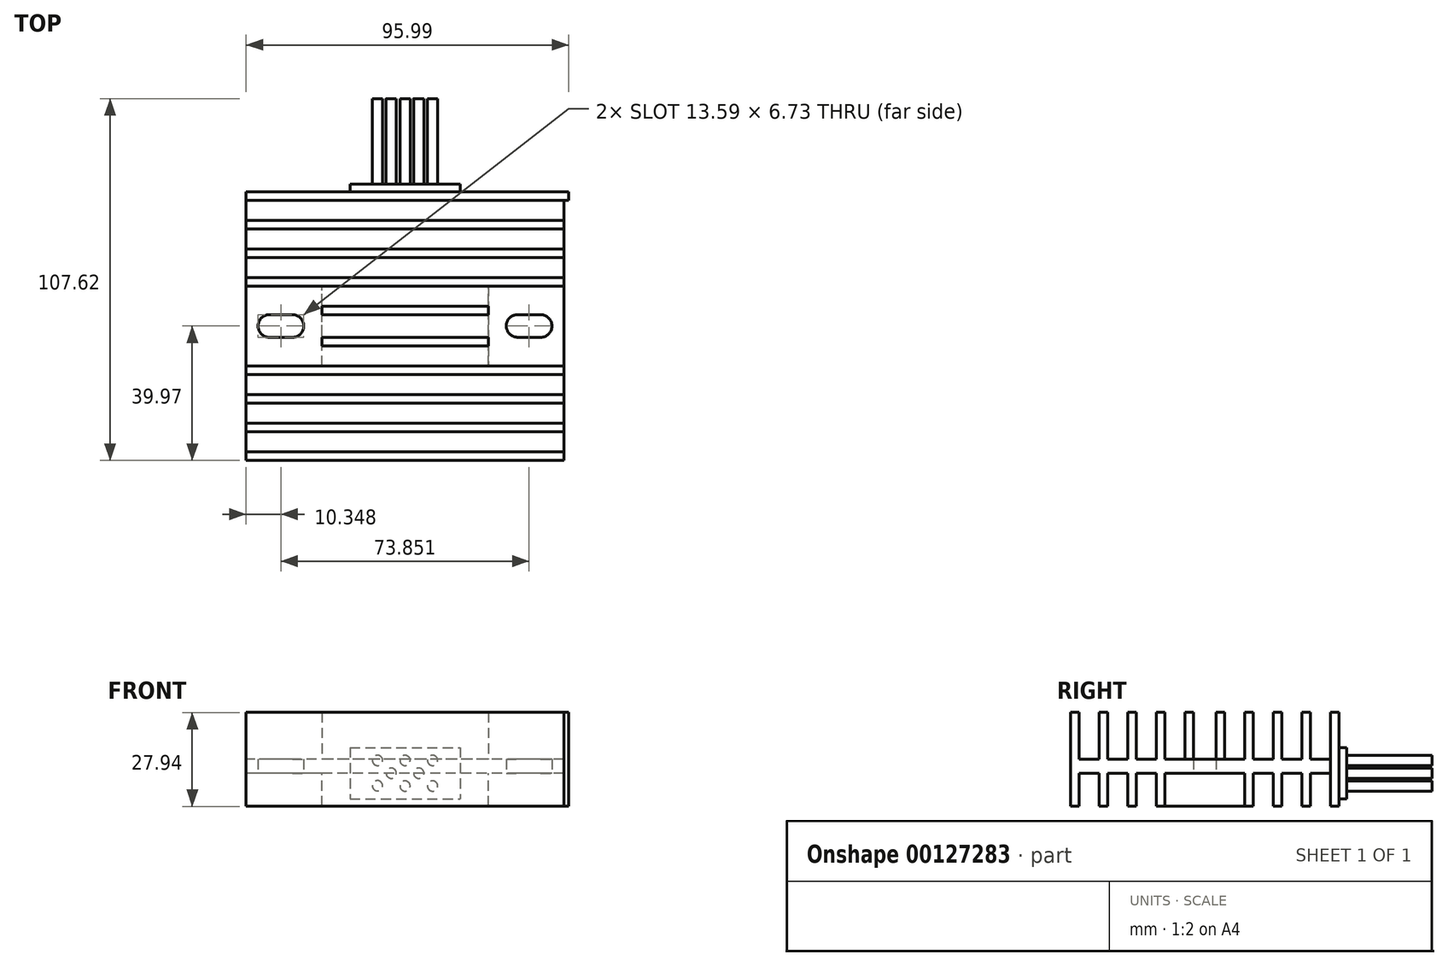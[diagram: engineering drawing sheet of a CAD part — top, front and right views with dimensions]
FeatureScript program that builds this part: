
annotation { "Feature Type Name" : "Feature", "Feature Type Description" : "" }
export const myFeature = defineFeature(function(context is Context, id is Id, definition is map)
    precondition{}
    {
        {
            var Q0;
            Q0=qCreatedBy(makeId("Top.planeOp"),FACE);
            var sketch = newSketch(context, id + "F0", { "sketchPlane" : qUnion([Q0])});
            skLineSegment(sketch, "E0.bottom", {"start": v(47.28, 39.97) * mm, "end": v(-47.28, 39.97) * mm});
            skLineSegment(sketch, "E0.top", {"start": v(47.28, -39.97) * mm, "end": v(-47.28, -39.97) * mm});
            skLineSegment(sketch, "E0.left", {"start": v(47.28, 39.97) * mm, "end": v(47.28, -39.97) * mm});
            skLineSegment(sketch, "E0.right", {"start": v(-47.28, 39.97) * mm, "end": v(-47.28, -39.97) * mm});
            skPoint(sketch, "E0.middle", {"position": v(0, 0) * mm});
            skLineSegment(sketch, "E1.bottom", {"start": v(-33.5, 3.37) * mm, "end": v(-40.36, 3.37) * mm});
            skLineSegment(sketch, "E1.top", {"start": v(-33.5, -3.37) * mm, "end": v(-40.36, -3.37) * mm});
            skPoint(sketch, "E1.middle", {"position": v(-36.93, 0) * mm});
            skArc(sketch, "E2", {"start": v(-40.36, 3.37) * mm, "mid": v(-43.73, 0) * mm, "end": v(-40.36, -3.37) * mm});
            skArc(sketch, "E3", {"start": v(-33.5, -3.37) * mm, "mid": v(-30.14, 0) * mm, "end": v(-33.5, 3.37) * mm});
            skLineSegment(sketch, "E4.bottom", {"start": v(40.36, 3.37) * mm, "end": v(33.5, 3.37) * mm});
            skLineSegment(sketch, "E4.top", {"start": v(40.35, -3.37) * mm, "end": v(33.49, -3.37) * mm});
            skArc(sketch, "E5", {"start": v(40.35, -3.37) * mm, "mid": v(43.71, 0) * mm, "end": v(40.36, 3.37) * mm});
            skArc(sketch, "E6", {"start": v(33.5, 3.37) * mm, "mid": v(30.12, 0) * mm, "end": v(33.49, -3.37) * mm});
            skSolve(sketch);
        }
        {
            var Q0;
            Q0=makeQuery(id+"F0.imprint","IMPRINT",FACE,{"disambiguationData":[TD([[makeQuery(id+"F0.imprint","IMPRINT",EDGE,{"derivedFrom":sQuery(id+"F0.wireOp",EDGE,"E0.bottom")}),1.0]])]});
            extrude(context, id + "F1", {"entities" : qUnion([Q0]), "depth" : 4.11 * mm});
        }
        {
            var Q0;
            Q0=makeQuery(id+"F1.opExtrude","CAP_FACE",FACE,{"disambiguationData":[OSD([sQuery(id+"F0.wireOp",EDGE,"E0.bottom"),sQuery(id+"F0.wireOp",EDGE,"E0.top"),sQuery(id+"F0.wireOp",EDGE,"E0.left"),sQuery(id+"F0.wireOp",EDGE,"E0.right"),sQuery(id+"F0.wireOp",EDGE,"E1.bottom"),sQuery(id+"F0.wireOp",EDGE,"E1.top"),sQuery(id+"F0.wireOp",EDGE,"E2"),sQuery(id+"F0.wireOp",EDGE,"E3"),sQuery(id+"F0.wireOp",EDGE,"E4.bottom"),sQuery(id+"F0.wireOp",EDGE,"E4.top"),sQuery(id+"F0.wireOp",EDGE,"E5"),sQuery(id+"F0.wireOp",EDGE,"E6")])],"isStart":false});
            var sketch = newSketch(context, id + "F2", { "sketchPlane" : qUnion([Q0])});
            skLineSegment(sketch, "E7.bottom", {"start": v(24.77, 39.97) * mm, "end": v(-24.77, 39.97) * mm});
            skLineSegment(sketch, "E7.top", {"start": v(24.77, -39.97) * mm, "end": v(-24.77, -39.97) * mm});
            skLineSegment(sketch, "E7.left", {"start": v(24.77, 39.97) * mm, "end": v(24.77, -39.97) * mm});
            skLineSegment(sketch, "E7.right", {"start": v(-24.77, 39.97) * mm, "end": v(-24.77, -39.97) * mm});
            skPoint(sketch, "E7.middle", {"position": v(0, 0) * mm});
            skLineSegment(sketch, "E8.bottom", {"start": v(-47.28, 39.97) * mm, "end": v(48.7, 39.97) * mm});
            skLineSegment(sketch, "E8.top", {"start": v(-47.28, 37.43) * mm, "end": v(48.7, 37.43) * mm});
            skLineSegment(sketch, "E8.left", {"start": v(-47.28, 39.97) * mm, "end": v(-47.28, 37.43) * mm});
            skLineSegment(sketch, "E8.right", {"start": v(48.7, 39.97) * mm, "end": v(48.7, 37.43) * mm});
            skLineSegment(sketch, "E9.bottom", {"start": v(-47.28, 31.46) * mm, "end": v(47.28, 31.46) * mm});
            skLineSegment(sketch, "E9.top", {"start": v(-47.28, 28.92) * mm, "end": v(47.28, 28.92) * mm});
            skLineSegment(sketch, "E9.left", {"start": v(-47.28, 31.46) * mm, "end": v(-47.28, 28.92) * mm});
            skLineSegment(sketch, "E9.right", {"start": v(47.28, 31.46) * mm, "end": v(47.28, 28.92) * mm});
            skLineSegment(sketch, "E10.bottom", {"start": v(-47.28, 22.95) * mm, "end": v(47.28, 22.95) * mm});
            skLineSegment(sketch, "E10.top", {"start": v(-47.28, 20.4) * mm, "end": v(47.28, 20.4) * mm});
            skLineSegment(sketch, "E10.left", {"start": v(-47.28, 22.95) * mm, "end": v(-47.28, 20.4) * mm});
            skLineSegment(sketch, "E10.right", {"start": v(47.28, 22.95) * mm, "end": v(47.28, 20.4) * mm});
            skLineSegment(sketch, "E11.bottom", {"start": v(-47.28, 14.44) * mm, "end": v(47.28, 14.44) * mm});
            skLineSegment(sketch, "E11.top", {"start": v(-47.28, 11.9) * mm, "end": v(47.28, 11.9) * mm});
            skLineSegment(sketch, "E11.left", {"start": v(-47.28, 14.44) * mm, "end": v(-47.28, 11.9) * mm});
            skLineSegment(sketch, "E11.right", {"start": v(47.28, 14.44) * mm, "end": v(47.28, 11.9) * mm});
            skLineSegment(sketch, "E12.bottom", {"start": v(-24.77, 5.93) * mm, "end": v(24.77, 5.93) * mm});
            skLineSegment(sketch, "E12.top", {"start": v(-24.77, 3.4) * mm, "end": v(24.77, 3.4) * mm});
            skLineSegment(sketch, "E12.left", {"start": v(-24.77, 5.93) * mm, "end": v(-24.77, 3.4) * mm});
            skLineSegment(sketch, "E12.right", {"start": v(24.77, 5.93) * mm, "end": v(24.77, 3.4) * mm});
            skLineSegment(sketch, "E13.bottom", {"start": v(-47.28, -39.97) * mm, "end": v(47.28, -39.97) * mm});
            skLineSegment(sketch, "E13.top", {"start": v(-47.28, -37.43) * mm, "end": v(47.28, -37.43) * mm});
            skLineSegment(sketch, "E13.left", {"start": v(-47.28, -39.97) * mm, "end": v(-47.28, -37.43) * mm});
            skLineSegment(sketch, "E13.right", {"start": v(47.28, -39.97) * mm, "end": v(47.28, -37.43) * mm});
            skLineSegment(sketch, "E14.bottom", {"start": v(-47.28, -31.46) * mm, "end": v(47.28, -31.46) * mm});
            skLineSegment(sketch, "E14.top", {"start": v(-47.28, -28.92) * mm, "end": v(47.28, -28.92) * mm});
            skLineSegment(sketch, "E14.left", {"start": v(-47.28, -31.46) * mm, "end": v(-47.28, -28.92) * mm});
            skLineSegment(sketch, "E14.right", {"start": v(47.28, -31.46) * mm, "end": v(47.28, -28.92) * mm});
            skLineSegment(sketch, "E15.bottom", {"start": v(-47.28, -22.95) * mm, "end": v(47.28, -22.95) * mm});
            skLineSegment(sketch, "E15.top", {"start": v(-47.28, -20.4) * mm, "end": v(47.28, -20.4) * mm});
            skLineSegment(sketch, "E15.left", {"start": v(-47.28, -22.95) * mm, "end": v(-47.28, -20.4) * mm});
            skLineSegment(sketch, "E15.right", {"start": v(47.28, -22.95) * mm, "end": v(47.28, -20.4) * mm});
            skLineSegment(sketch, "E16.bottom", {"start": v(-47.28, -14.44) * mm, "end": v(47.28, -14.44) * mm});
            skLineSegment(sketch, "E16.top", {"start": v(-47.28, -11.9) * mm, "end": v(47.28, -11.9) * mm});
            skLineSegment(sketch, "E16.left", {"start": v(-47.28, -14.44) * mm, "end": v(-47.28, -11.9) * mm});
            skLineSegment(sketch, "E16.right", {"start": v(47.28, -14.44) * mm, "end": v(47.28, -11.9) * mm});
            skLineSegment(sketch, "E17.bottom", {"start": v(-24.77, -5.93) * mm, "end": v(24.77, -5.93) * mm});
            skLineSegment(sketch, "E17.top", {"start": v(-24.77, -3.4) * mm, "end": v(24.77, -3.4) * mm});
            skLineSegment(sketch, "E17.left", {"start": v(-24.77, -5.93) * mm, "end": v(-24.77, -3.4) * mm});
            skLineSegment(sketch, "E17.right", {"start": v(24.77, -5.93) * mm, "end": v(24.77, -3.4) * mm});
            skSolve(sketch);
        }
        {
            var Q0;
            {var subQ5=sQuery(id+"F2.wireOp",EDGE,"E13.right");Q0=makeQuery(id+"F2.imprint","IMPRINT",FACE,{"disambiguationData":[TD([[makeQuery(id+"F2.imprint","IMPRINT",EDGE,{"derivedFrom":subQ5}),-1.0]])]});}
            var Q1;
            {var subQ5=sQuery(id+"F2.wireOp",EDGE,"E8.left");Q1=makeQuery(id+"F2.imprint","IMPRINT",FACE,{"disambiguationData":[TD([[makeQuery(id+"F2.imprint","IMPRINT",EDGE,{"derivedFrom":subQ5}),1.0]])]});}
            var Q2;
            {var subQ5=sQuery(id+"F2.wireOp",EDGE,"E13.left");Q2=makeQuery(id+"F2.imprint","IMPRINT",FACE,{"disambiguationData":[TD([[makeQuery(id+"F2.imprint","IMPRINT",EDGE,{"derivedFrom":subQ5}),1.0]])]});}
            var Q3;
            {var subQ0=sQuery(id+"F2.wireOp",EDGE,"E8.bottom");var subQ1=sQuery(id+"F2.wireOp",EDGE,"E7.left");var subQ2=makeQuery(id+"F2.imprint","INTERSECT",VERTEX,{"derivedFrom":[subQ1,subQ0]});Q3=makeQuery(id+"F2.imprint","IMPRINT",FACE,{"disambiguationData":[TD([[makeQuery(id+"F2.imprint","IMPRINT",EDGE,{"disambiguationData":[TD([[subQ2,-1.0]])],"derivedFrom":subQ1}),-1.0]])]});}
            var Q4;
            {var subQ5=sQuery(id+"F2.wireOp",EDGE,"E9.right");Q4=makeQuery(id+"F2.imprint","IMPRINT",FACE,{"disambiguationData":[TD([[makeQuery(id+"F2.imprint","IMPRINT",EDGE,{"derivedFrom":subQ5}),-1.0]])]});}
            var Q5;
            {var subQ5=sQuery(id+"F2.wireOp",EDGE,"E10.right");Q5=makeQuery(id+"F2.imprint","IMPRINT",FACE,{"disambiguationData":[TD([[makeQuery(id+"F2.imprint","IMPRINT",EDGE,{"derivedFrom":subQ5}),-1.0]])]});}
            var Q6;
            {var subQ5=sQuery(id+"F2.wireOp",EDGE,"E11.right");Q6=makeQuery(id+"F2.imprint","IMPRINT",FACE,{"disambiguationData":[TD([[makeQuery(id+"F2.imprint","IMPRINT",EDGE,{"derivedFrom":subQ5}),-1.0]])]});}
            var Q7;
            {var subQ5=sQuery(id+"F2.wireOp",EDGE,"E16.right");Q7=makeQuery(id+"F2.imprint","IMPRINT",FACE,{"disambiguationData":[TD([[makeQuery(id+"F2.imprint","IMPRINT",EDGE,{"derivedFrom":subQ5}),-1.0]])]});}
            var Q8;
            {var subQ5=sQuery(id+"F2.wireOp",EDGE,"E15.right");Q8=makeQuery(id+"F2.imprint","IMPRINT",FACE,{"disambiguationData":[TD([[makeQuery(id+"F2.imprint","IMPRINT",EDGE,{"derivedFrom":subQ5}),-1.0]])]});}
            var Q9;
            {var subQ5=sQuery(id+"F2.wireOp",EDGE,"E14.right");Q9=makeQuery(id+"F2.imprint","IMPRINT",FACE,{"disambiguationData":[TD([[makeQuery(id+"F2.imprint","IMPRINT",EDGE,{"derivedFrom":subQ5}),-1.0]])]});}
            var Q10;
            {var subQ0=sQuery(id+"F2.wireOp",EDGE,"E13.bottom");var subQ1=sQuery(id+"F2.wireOp",EDGE,"E7.left");var subQ2=makeQuery(id+"F2.imprint","INTERSECT",VERTEX,{"derivedFrom":[subQ1,subQ0]});Q10=makeQuery(id+"F2.imprint","IMPRINT",FACE,{"disambiguationData":[TD([[makeQuery(id+"F2.imprint","IMPRINT",EDGE,{"disambiguationData":[TD([[subQ2,1.0]])],"derivedFrom":subQ1}),-1.0]])]});}
            var Q11;
            {var subQ5=sQuery(id+"F2.wireOp",EDGE,"E9.left");Q11=makeQuery(id+"F2.imprint","IMPRINT",FACE,{"disambiguationData":[TD([[makeQuery(id+"F2.imprint","IMPRINT",EDGE,{"derivedFrom":subQ5}),1.0]])]});}
            var Q12;
            {var subQ5=sQuery(id+"F2.wireOp",EDGE,"E10.left");Q12=makeQuery(id+"F2.imprint","IMPRINT",FACE,{"disambiguationData":[TD([[makeQuery(id+"F2.imprint","IMPRINT",EDGE,{"derivedFrom":subQ5}),1.0]])]});}
            var Q13;
            {var subQ5=sQuery(id+"F2.wireOp",EDGE,"E11.left");Q13=makeQuery(id+"F2.imprint","IMPRINT",FACE,{"disambiguationData":[TD([[makeQuery(id+"F2.imprint","IMPRINT",EDGE,{"derivedFrom":subQ5}),1.0]])]});}
            var Q14;
            {var subQ5=sQuery(id+"F2.wireOp",EDGE,"E16.left");Q14=makeQuery(id+"F2.imprint","IMPRINT",FACE,{"disambiguationData":[TD([[makeQuery(id+"F2.imprint","IMPRINT",EDGE,{"derivedFrom":subQ5}),1.0]])]});}
            var Q15;
            {var subQ5=sQuery(id+"F2.wireOp",EDGE,"E15.left");Q15=makeQuery(id+"F2.imprint","IMPRINT",FACE,{"disambiguationData":[TD([[makeQuery(id+"F2.imprint","IMPRINT",EDGE,{"derivedFrom":subQ5}),1.0]])]});}
            var Q16;
            {var subQ5=sQuery(id+"F2.wireOp",EDGE,"E14.left");Q16=makeQuery(id+"F2.imprint","IMPRINT",FACE,{"disambiguationData":[TD([[makeQuery(id+"F2.imprint","IMPRINT",EDGE,{"derivedFrom":subQ5}),1.0]])]});}
            var Q17;
            {var subQ0=sQuery(id+"F2.wireOp",EDGE,"E9.bottom");var subQ1=sQuery(id+"F2.wireOp",EDGE,"E7.left");var subQ2=makeQuery(id+"F2.imprint","INTERSECT",VERTEX,{"derivedFrom":[subQ1,subQ0]});Q17=makeQuery(id+"F2.imprint","IMPRINT",FACE,{"disambiguationData":[TD([[makeQuery(id+"F2.imprint","IMPRINT",EDGE,{"disambiguationData":[TD([[subQ2,-1.0]])],"derivedFrom":subQ1}),-1.0]])]});}
            var Q18;
            {var subQ0=sQuery(id+"F2.wireOp",EDGE,"E10.bottom");var subQ1=sQuery(id+"F2.wireOp",EDGE,"E7.left");var subQ2=makeQuery(id+"F2.imprint","INTERSECT",VERTEX,{"derivedFrom":[subQ1,subQ0]});Q18=makeQuery(id+"F2.imprint","IMPRINT",FACE,{"disambiguationData":[TD([[makeQuery(id+"F2.imprint","IMPRINT",EDGE,{"disambiguationData":[TD([[subQ2,-1.0]])],"derivedFrom":subQ1}),-1.0]])]});}
            var Q19;
            {var subQ0=sQuery(id+"F2.wireOp",EDGE,"E11.bottom");var subQ1=sQuery(id+"F2.wireOp",EDGE,"E7.left");var subQ2=makeQuery(id+"F2.imprint","INTERSECT",VERTEX,{"derivedFrom":[subQ1,subQ0]});Q19=makeQuery(id+"F2.imprint","IMPRINT",FACE,{"disambiguationData":[TD([[makeQuery(id+"F2.imprint","IMPRINT",EDGE,{"disambiguationData":[TD([[subQ2,-1.0]])],"derivedFrom":subQ1}),-1.0]])]});}
            var Q20;
            {var subQ0=sQuery(id+"F2.wireOp",EDGE,"E16.top");var subQ1=sQuery(id+"F2.wireOp",EDGE,"E7.left");var subQ2=makeQuery(id+"F2.imprint","INTERSECT",VERTEX,{"derivedFrom":[subQ1,subQ0]});Q20=makeQuery(id+"F2.imprint","IMPRINT",FACE,{"disambiguationData":[TD([[makeQuery(id+"F2.imprint","IMPRINT",EDGE,{"disambiguationData":[TD([[subQ2,-1.0]])],"derivedFrom":subQ1}),-1.0]])]});}
            var Q21;
            {var subQ0=sQuery(id+"F2.wireOp",EDGE,"E15.top");var subQ1=sQuery(id+"F2.wireOp",EDGE,"E7.left");var subQ2=makeQuery(id+"F2.imprint","INTERSECT",VERTEX,{"derivedFrom":[subQ1,subQ0]});Q21=makeQuery(id+"F2.imprint","IMPRINT",FACE,{"disambiguationData":[TD([[makeQuery(id+"F2.imprint","IMPRINT",EDGE,{"disambiguationData":[TD([[subQ2,-1.0]])],"derivedFrom":subQ1}),-1.0]])]});}
            var Q22;
            {var subQ0=sQuery(id+"F2.wireOp",EDGE,"E14.top");var subQ1=sQuery(id+"F2.wireOp",EDGE,"E7.left");var subQ2=makeQuery(id+"F2.imprint","INTERSECT",VERTEX,{"derivedFrom":[subQ1,subQ0]});Q22=makeQuery(id+"F2.imprint","IMPRINT",FACE,{"disambiguationData":[TD([[makeQuery(id+"F2.imprint","IMPRINT",EDGE,{"disambiguationData":[TD([[subQ2,-1.0]])],"derivedFrom":subQ1}),-1.0]])]});}
            var Q23;
            Q23=makeQuery(id+"F2.imprint","IMPRINT",FACE,{"disambiguationData":[TD([[makeQuery(id+"F2.imprint","IMPRINT",EDGE,{"derivedFrom":sQuery(id+"F2.wireOp",EDGE,"E12.bottom")}),-1.0]])]});
            var Q24;
            Q24=makeQuery(id+"F2.imprint","IMPRINT",FACE,{"disambiguationData":[TD([[makeQuery(id+"F2.imprint","IMPRINT",EDGE,{"derivedFrom":sQuery(id+"F2.wireOp",EDGE,"E17.bottom")}),1.0]])]});
            var Q25;
            {var subQ3=sQuery(id+"F2.wireOp",EDGE,"E8.right");Q25=makeQuery(id+"F2.imprint","IMPRINT",FACE,{"disambiguationData":[TD([[makeQuery(id+"F2.imprint","IMPRINT",EDGE,{"derivedFrom":subQ3}),-1.0]])]});}
            var Q26;
            {var subQ0=sQuery(id+"F2.wireOp",EDGE,"E8.bottom");var subQ1=sQuery(id+"F2.wireOp",EDGE,"E7.left");var subQ2=makeQuery(id+"F2.imprint","INTERSECT",VERTEX,{"derivedFrom":[subQ1,subQ0]});Q26=makeQuery(id+"F2.imprint","IMPRINT",FACE,{"disambiguationData":[TD([[makeQuery(id+"F2.imprint","IMPRINT",EDGE,{"disambiguationData":[TD([[subQ2,-1.0]])],"derivedFrom":subQ1}),1.0]])]});}
            extrude(context, id + "F3", {"entities" : qUnion([Q0, Q1, Q2, Q3, Q4, Q5, Q6, Q7, Q8, Q9, Q10, Q11, Q12, Q13, Q14, Q15, Q16, Q17, Q18, Q19, Q20, Q21, Q22, Q23, Q24, Q25, Q26]), "operationType" : NewBodyOperationType.ADD, "endBound" : BoundingType.SYMMETRIC, "depth" : 27.94 * mm, "hasSecondDirection" : true, "secondDirectionOppositeDirection" : true, "secondDirectionDepth" : 25.4 * mm});
        }
        {
            var Q0;
            Q0=makeQuery(id+"F3.boolean.opBoolean","MERGE",FACE,{"derivedFrom":[makeQuery(id+"F1.opExtrude","SWEPT_FACE",FACE,{"disambiguationData":[OSD([sQuery(id+"F0.wireOp",EDGE,"E0.bottom")])]}),makeQuery(id+"F3.opExtrude","SWEPT_FACE",FACE,{"disambiguationData":[OSD([sQuery(id+"F2.wireOp",EDGE,"E8.bottom")])]})]});
            var sketch = newSketch(context, id + "F4", { "sketchPlane" : qUnion([Q0])});
            skLineSegment(sketch, "E18.bottom", {"start": v(16.38, 7.62) * mm, "end": v(-16.38, 7.62) * mm});
            skLineSegment(sketch, "E18.top", {"start": v(16.38, -7.62) * mm, "end": v(-16.38, -7.62) * mm});
            skLineSegment(sketch, "E18.left", {"start": v(16.38, 7.62) * mm, "end": v(16.38, -7.62) * mm});
            skLineSegment(sketch, "E18.right", {"start": v(-16.38, 7.62) * mm, "end": v(-16.38, -7.62) * mm});
            skPoint(sketch, "E18.middle", {"position": v(0, 0) * mm});
            skSolve(sketch);
        }
        {
            var Q0;
            Q0=makeQuery(id+"F4.imprint","IMPRINT",FACE,{"disambiguationData":[TD([[makeQuery(id+"F4.imprint","IMPRINT",EDGE,{"derivedFrom":sQuery(id+"F4.wireOp",EDGE,"E18.bottom")}),1.0]])]});
            extrude(context, id + "F5", {"entities" : qUnion([Q0]), "operationType" : NewBodyOperationType.ADD, "depth" : 2.3 * mm});
        }
        {
            var Q0;
            Q0=makeQuery(id+"F5.opExtrude","CAP_FACE",FACE,{"disambiguationData":[OSD([sQuery(id+"F4.wireOp",EDGE,"E18.bottom"),sQuery(id+"F4.wireOp",EDGE,"E18.top"),sQuery(id+"F4.wireOp",EDGE,"E18.left"),sQuery(id+"F4.wireOp",EDGE,"E18.right")])],"isStart":false});
            var sketch = newSketch(context, id + "F6", { "sketchPlane" : qUnion([Q0])});
            skCircle(sketch, "E19", {"center": v(-8.2, 3.8) * mm, "radius": 1.52 * mm});
            skCircle(sketch, "E20", {"center": v(8.2, 3.81) * mm, "radius": 1.52 * mm});
            skCircle(sketch, "E21", {"center": v(4.1, 0) * mm, "radius": 1.52 * mm});
            skCircle(sketch, "E22", {"center": v(-4.1, 0) * mm, "radius": 1.52 * mm});
            skCircle(sketch, "E23", {"center": v(8.2, -3.73) * mm, "radius": 1.52 * mm});
            skCircle(sketch, "E24", {"center": v(-8.2, -3.81) * mm, "radius": 1.52 * mm});
            skCircle(sketch, "E25", {"center": v(0, 3.81) * mm, "radius": 1.52 * mm});
            skCircle(sketch, "E26", {"center": v(0, -3.81) * mm, "radius": 1.52 * mm});
            skSolve(sketch);
        }
        {
            var Q0;
            {var subQ0=sQuery(id+"F0.wireOp",EDGE,"E5");var subQ1=sQuery(id+"F0.wireOp",EDGE,"E1.top");var subQ2=sQuery(id+"F0.wireOp",EDGE,"E1.bottom");var subQ3=sQuery(id+"F0.wireOp",EDGE,"E0.right");var subQ4=sQuery(id+"F0.wireOp",EDGE,"E0.left");var subQ5=sQuery(id+"F0.wireOp",EDGE,"E2");var subQ6=sQuery(id+"F0.wireOp",EDGE,"E3");var subQ7=sQuery(id+"F0.wireOp",EDGE,"E6");var subQ8=sQuery(id+"F0.wireOp",EDGE,"E4.bottom");var subQ9=sQuery(id+"F0.wireOp",EDGE,"E4.top");Q0=makeQuery(id+"F3.boolean.opBoolean","SPLIT",FACE,{"disambiguationData":[TD([makeQuery(id+"F1.opExtrude","SWEPT_FACE",FACE,{"disambiguationData":[OSD([subQ2])]})])],"derivedFrom":makeQuery(id+"F1.opExtrude","CAP_FACE",FACE,{"disambiguationData":[OSD([sQuery(id+"F0.wireOp",EDGE,"E0.bottom"),sQuery(id+"F0.wireOp",EDGE,"E0.top"),subQ4,subQ3,subQ2,subQ1,subQ5,subQ6,subQ8,subQ9,subQ0,subQ7])],"isStart":true})});}
            var sketch = newSketch(context, id + "F7", { "sketchPlane" : qUnion([Q0])});
            skLineSegment(sketch, "E27", {"start": v(-24.77, 11.9) * mm, "end": v(-24.77, -11.9) * mm});
            skLineSegment(sketch, "E28", {"start": v(-24.77, -11.9) * mm, "end": v(24.77, -11.9) * mm});
            skLineSegment(sketch, "E29", {"start": v(24.77, -11.9) * mm, "end": v(24.77, 11.9) * mm});
            skSolve(sketch);
        }
        {
            var Q0;
            Q0 = qSketchRegion(id + "F7", true);
            var Q1;
            {var subQ1=makeQuery(id+"F1.opExtrude","CAP_FACE",FACE,{"disambiguationData":[OSD([sQuery(id+"F0.wireOp",EDGE,"E0.bottom"),sQuery(id+"F0.wireOp",EDGE,"E0.top"),sQuery(id+"F0.wireOp",EDGE,"E0.left"),sQuery(id+"F0.wireOp",EDGE,"E0.right"),sQuery(id+"F0.wireOp",EDGE,"E1.bottom"),sQuery(id+"F0.wireOp",EDGE,"E1.top"),sQuery(id+"F0.wireOp",EDGE,"E2"),sQuery(id+"F0.wireOp",EDGE,"E3"),sQuery(id+"F0.wireOp",EDGE,"E4.bottom"),sQuery(id+"F0.wireOp",EDGE,"E4.top"),sQuery(id+"F0.wireOp",EDGE,"E5"),sQuery(id+"F0.wireOp",EDGE,"E6")])],"isStart":true});var subQ2=makeQuery(id+"F3.boolean.opBoolean","INTERSECT",EDGE,{"derivedFrom":[subQ1,makeQuery(id+"F3.opExtrude","SWEPT_FACE",FACE,{"disambiguationData":[OSD([sQuery(id+"F2.wireOp",EDGE,"E12.top")])]})]});Q1=makeQuery(id+"F7.imprint","IMPRINT",FACE,{"disambiguationData":[TD([[makeQuery(id+"F7.imprint","IMPRINT",EDGE,{"derivedFrom":subQ2}),-1.0]])]});}
            var Q2;
            {var subQ1=makeQuery(id+"F1.opExtrude","CAP_FACE",FACE,{"disambiguationData":[OSD([sQuery(id+"F0.wireOp",EDGE,"E0.bottom"),sQuery(id+"F0.wireOp",EDGE,"E0.top"),sQuery(id+"F0.wireOp",EDGE,"E0.left"),sQuery(id+"F0.wireOp",EDGE,"E0.right"),sQuery(id+"F0.wireOp",EDGE,"E1.bottom"),sQuery(id+"F0.wireOp",EDGE,"E1.top"),sQuery(id+"F0.wireOp",EDGE,"E2"),sQuery(id+"F0.wireOp",EDGE,"E3"),sQuery(id+"F0.wireOp",EDGE,"E4.bottom"),sQuery(id+"F0.wireOp",EDGE,"E4.top"),sQuery(id+"F0.wireOp",EDGE,"E5"),sQuery(id+"F0.wireOp",EDGE,"E6")])],"isStart":true});var subQ2=makeQuery(id+"F3.boolean.opBoolean","INTERSECT",EDGE,{"derivedFrom":[subQ1,makeQuery(id+"F3.opExtrude","SWEPT_FACE",FACE,{"disambiguationData":[OSD([sQuery(id+"F2.wireOp",EDGE,"E17.bottom")])]})]});Q2=makeQuery(id+"F7.imprint","IMPRINT",FACE,{"disambiguationData":[TD([[makeQuery(id+"F7.imprint","IMPRINT",EDGE,{"derivedFrom":subQ2}),-1.0]])]});}
            var Q3;
            {var subQ3=sQuery(id+"F7.wireOp",EDGE,"E28");Q3=makeQuery(id+"F7.imprint","IMPRINT",FACE,{"disambiguationData":[TD([[makeQuery(id+"F7.imprint","IMPRINT",EDGE,{"derivedFrom":subQ3}),-1.0]])]});}
            extrude(context, id + "F8", {"entities" : qUnion([Q0, Q1, Q2, Q3]), "operationType" : NewBodyOperationType.ADD, "depth" : 9.78 * mm});
        }
        {
            var Q0;
            Q0 = qSketchRegion(id + "F6", true);
            extrude(context, id + "F9", {"entities" : qUnion([Q0]), "operationType" : NewBodyOperationType.ADD, "depth" : 25.4 * mm});
        }
    });
